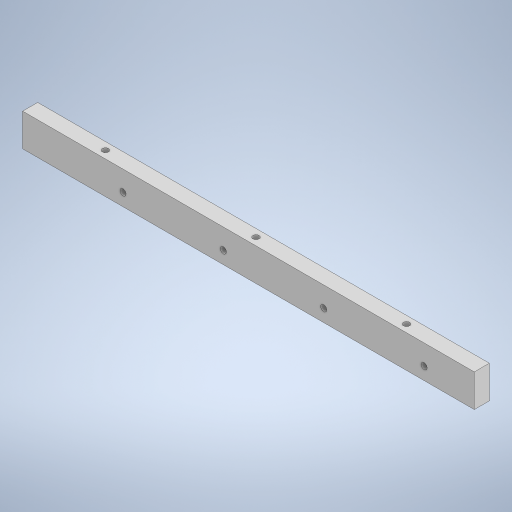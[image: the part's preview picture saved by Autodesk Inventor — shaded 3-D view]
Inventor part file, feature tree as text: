
AUTODESK INVENTOR PART (.ipt)
format: ipt  version: 2023 (Build 270158000, 158)  size: 249,344 bytes
history: native  units: mm
features: sketch x3, hole x2, other x1, extrude x1
ambient origin geometry x8: Origin, YZ Plane, XZ Plane, XY Plane, X Axis, Y Axis, Z Axis, Center Point
bodies: Body1 (feature_tree)
feature tree (7):
  other  "ソリッド1"
  extrude  "押し出し1"  Depth=180.0mm
  hole  "穴1"  [1 undecoded]
  hole  "穴2"  [1 undecoded]
  sketch  "スケッチ2"
  sketch  "スケッチ3"
  sketch  "スケッチ4"
note: 2 required parameter values undecoded (feature->parameter linkage not recoverable at this tier; creation-order binding heuristic only, values carry confidence <= 0.55)
